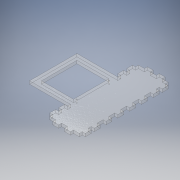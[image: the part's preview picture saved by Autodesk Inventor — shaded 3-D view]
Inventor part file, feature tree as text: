
AUTODESK INVENTOR PART (.ipt)
format: ipt  version: 2019 (Build 230136000, 136)  size: 215,552 bytes
history: native  units: mm
features: extrude x1, sketch x1
ambient origin geometry x8: Origin, YZ Plane, XZ Plane, XY Plane, X Axis, Y Axis, Z Axis, Center Point
bodies: Solid1 (feature_tree)
feature tree (2):
  extrude  "Extrusion1"  Depth=180.0mm
  sketch  "Sketch1"  dims[d0=60.0mm d1=180.0mm d2=6.0mm d3=6.0mm d4=12.0mm d5=12.0mm d6=12.0mm d7=12.0mm d8=12.0mm d9=6.0mm d10=12.0mm d15=6.0mm d16=0.0mm d17=6.0mm d19=6.0mm d20=6.0mm d21=6.0mm d22=12.0mm d23=12.0mm d24=12.0mm d25=6.0mm d26=65.0mm d27=12.0mm d28=2.3mm d29=3.45mm d30=3.0mm]
